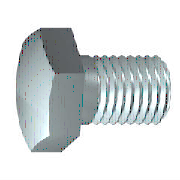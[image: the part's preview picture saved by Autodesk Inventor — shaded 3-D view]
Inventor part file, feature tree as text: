
AUTODESK INVENTOR PART (.ipt)
format: ipt  version: 2023.2 (Build 272271030, 271C)  size: 211,968 bytes
history: native  units: mm (DEFAULTED — no unit token found)
features: sketch x4, other x3, revolve x2, extrude x2, fillet x1
ambient origin geometry x8: Origin, YZ Plane, XZ Plane, XY Plane, X Axis, Y Axis, Z Axis, Center Point
bodies: Solid1 (feature_tree)
feature tree (12):
  revolve  "Revolution1"  Angle=45.0deg
  extrude  "Extrusion1"  TaperAngle=60.0deg  [1 undecoded]
  revolve  "Revolution2"  Angle=30.0deg
  extrude  "Extrusion2"  TaperAngle=0.0deg  [1 undecoded]
  other  "MSC_A1"
  other  "MSC_PF1"
  other  "MSC_PT1"
  fillet  "Fillet1"  [1 undecoded]
  sketch  "Sketch2"  dims[d3=30.0deg d5=45.0deg]
  sketch  "Sketch3"  dims[d8=90.0deg d9=60.0deg]
  sketch  "Sketch4"  dims[d13=0.0mm d14=30.0deg]
  sketch  "Sketch5"  dims[d16=90.0deg d18=0.0mm d22=0.0mm d23=0.0mm d25=0.0mm d26=0.0mm d27=13.5mm d28=1.5mm d29=0.0mm d30=0.6mm d31=0.0mm]
note: 3 required parameter values undecoded (feature->parameter linkage not recoverable at this tier; creation-order binding heuristic only, values carry confidence <= 0.55)
